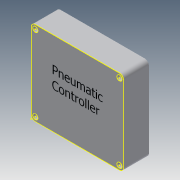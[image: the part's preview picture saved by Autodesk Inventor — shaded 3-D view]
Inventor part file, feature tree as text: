
AUTODESK INVENTOR PART (.ipt)
format: ipt  version: 2014 (Build 180170000, 170)  size: 100,864 bytes
history: native  units: in
note: dims shown in document units (in); Inventor stores cm internally (conversion verified against a paired STEP export)
features: sketch x3, extrude x1, fillet x1, hole x1
ambient origin geometry x8: Origin, YZ Plane, XZ Plane, XY Plane, X Axis, Y Axis, Z Axis, Center Point
bodies: Solid1 (feature_tree)
feature tree (6):
  extrude  "Extrusion1"  Depth=2.5in
  fillet  "Fillet1"  Radius=0.75in
  hole  "Hole1"  [1 undecoded]
  sketch  "Sketch3"  dims[d5=0.156in d6=0.75in d7=0.375in d8=0.25in d9=0.5635in d10=1.0in d11=0.8108in]
  sketch  "Sketch1"  dims[d0=2.75in d1=2.5in d2=0.75in d3=0.0in]
  sketch  "Sketch2"  dims[d4=0.125in]
note: 1 required parameter value undecoded (feature->parameter linkage not recoverable at this tier; creation-order binding heuristic only, values carry confidence <= 0.55)
